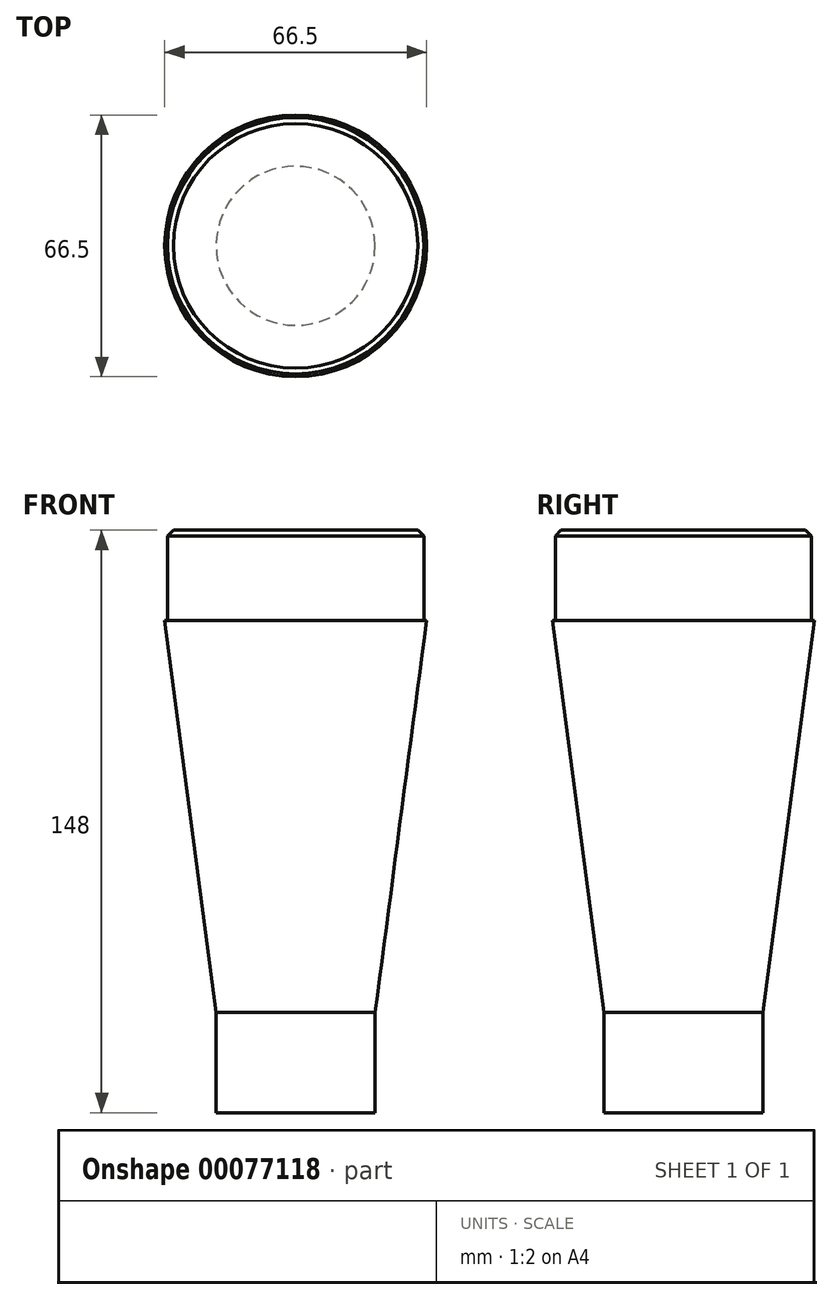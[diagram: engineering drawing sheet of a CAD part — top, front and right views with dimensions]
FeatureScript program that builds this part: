
annotation { "Feature Type Name" : "Feature", "Feature Type Description" : "" }
export const myFeature = defineFeature(function(context is Context, id is Id, definition is map)
    precondition{}
    {
        {
            var Q0;
            Q0=qCreatedBy(makeId("Front.planeOp"),FACE);
            var sketch = newSketch(context, id + "F0", { "sketchPlane" : qUnion([Q0])});
            skLineSegment(sketch, "E0", {"start": v(-32.55, 66.27) * mm, "end": v(-32.55, 43.27) * mm});
            skLineSegment(sketch, "E1", {"start": v(-32.55, 43.27) * mm, "end": v(-33.25, 43.27) * mm});
            skLineSegment(sketch, "E2", {"start": v(-33.25, 43.27) * mm, "end": v(-20.2, -56.31) * mm});
            skLineSegment(sketch, "E3", {"start": v(-20.2, -56.31) * mm, "end": v(-20.2, -81.73) * mm});
            skLineSegment(sketch, "E4", {"start": v(-20.2, -81.73) * mm, "end": v(0, -81.73) * mm});
            skLineSegment(sketch, "E5", {"start": v(-32.55, 66.27) * mm, "end": v(0, 66.27) * mm});
            skLineSegment(sketch, "E6", {"start": v(0, 94.78) * mm, "end": v(0, -99.97) * mm, "construction": true});
            skLineSegment(sketch, "E7", {"start": v(0, 66.27) * mm, "end": v(0, -81.73) * mm});
            skPoint(sketch, "E8.start.orphan", {"position": v(-20.8, -51.73) * mm});
            skPoint(sketch, "E9.orphan", {"position": v(-20.2, -48.73) * mm});
            skSolve(sketch);
        }
        {
            var Q0;
            Q0=makeQuery(id+"F0.imprint","IMPRINT",FACE,{"disambiguationData":[TD([[makeQuery(id+"F0.imprint","IMPRINT",EDGE,{"derivedFrom":sQuery(id+"F0.wireOp",EDGE,"E0")}),1.0]])]});
            var Q1;
            Q1=sQuery(id+"F0.wireOp",EDGE,"E6");
            revolve(context, id + "F1", {"entities" : qUnion([Q0]), "axis" : qUnion([Q1]), "revolveType" : RevolveType.FULL});
        }
        {
            var Q0;
            Q0=makeQuery(id+"F1.opRevolve","SWEPT_EDGE",EDGE,{"disambiguationData":[OSD([sQuery(id+"F0.wireOp",EDGE,"E0"),sQuery(id+"F0.wireOp",EDGE,"E5")])]});
            chamfer(context, id + "F2", {"entities" : qUnion([Q0]), "width" : 1.5 * mm, "tangentPropagation" : true});
        }
    });
